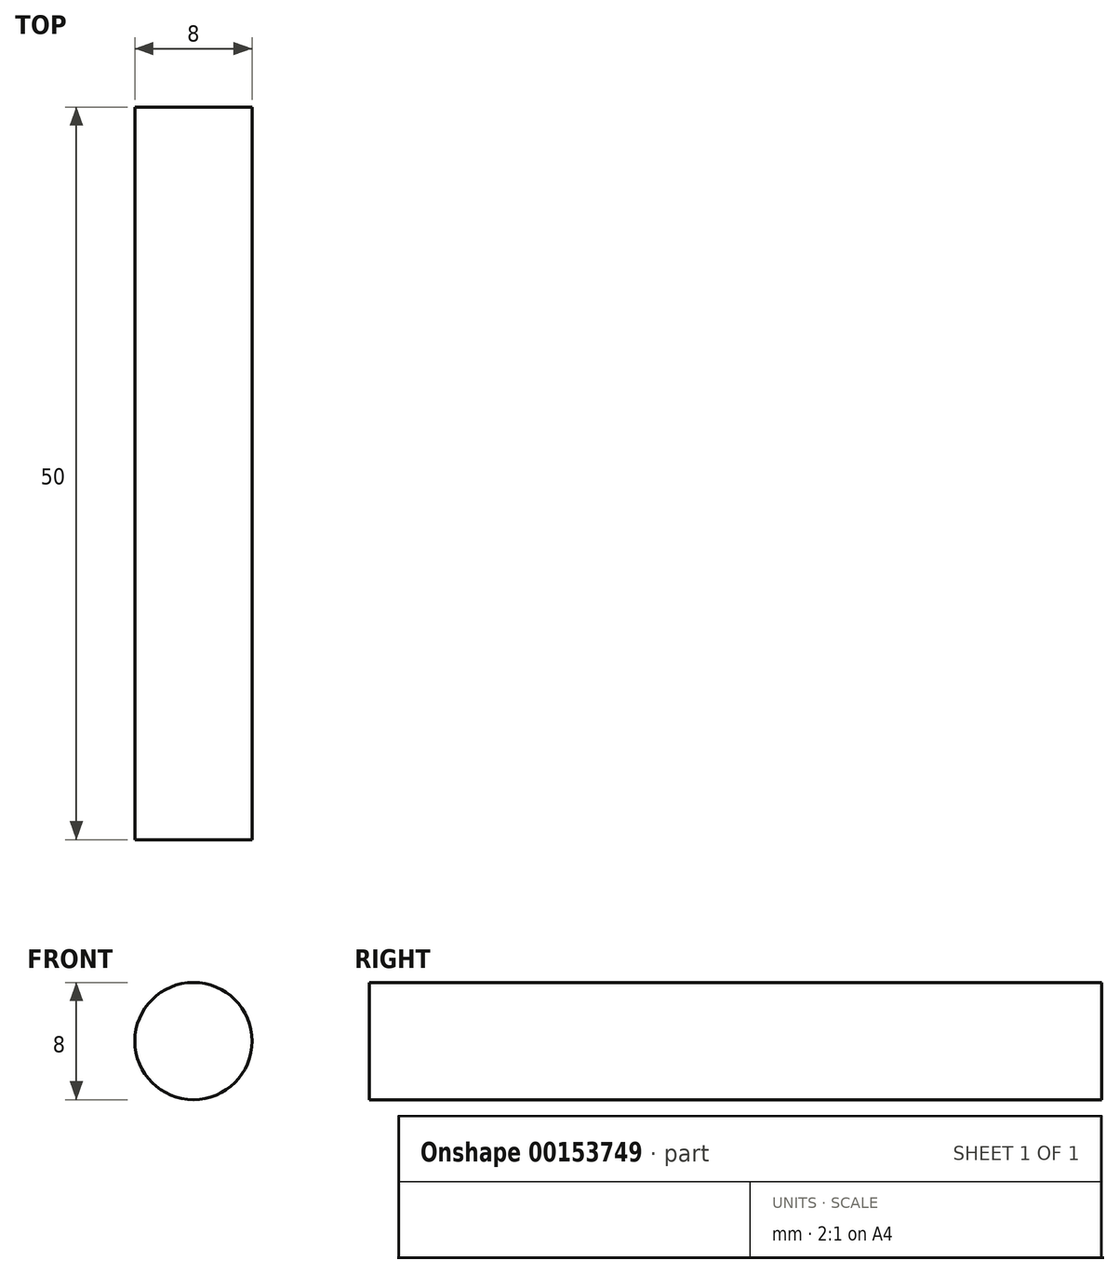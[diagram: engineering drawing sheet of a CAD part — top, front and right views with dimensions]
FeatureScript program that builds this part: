
annotation { "Feature Type Name" : "Feature", "Feature Type Description" : "" }
export const myFeature = defineFeature(function(context is Context, id is Id, definition is map)
    precondition{}
    {
        {
            var Q0;
            Q0=qCreatedBy(makeId("Front.planeOp"),FACE);
            var sketch = newSketch(context, id + "F0", { "sketchPlane" : qUnion([Q0])});
            skCircle(sketch, "E0", {"center": v(0, 0) * mm, "radius": 4 * mm});
            skSolve(sketch);
        }
        {
            var Q0;
            Q0=makeQuery(id+"F0.imprint","IMPRINT",FACE,{"disambiguationData":[TD([[makeQuery(id+"F0.imprint","IMPRINT",EDGE,{"derivedFrom":sQuery(id+"F0.wireOp",EDGE,"E0")}),1.0]])]});
            extrude(context, id + "F1", {"entities" : qUnion([Q0]), "oppositeDirection" : true, "depth" : 50 * mm});
        }
    });
